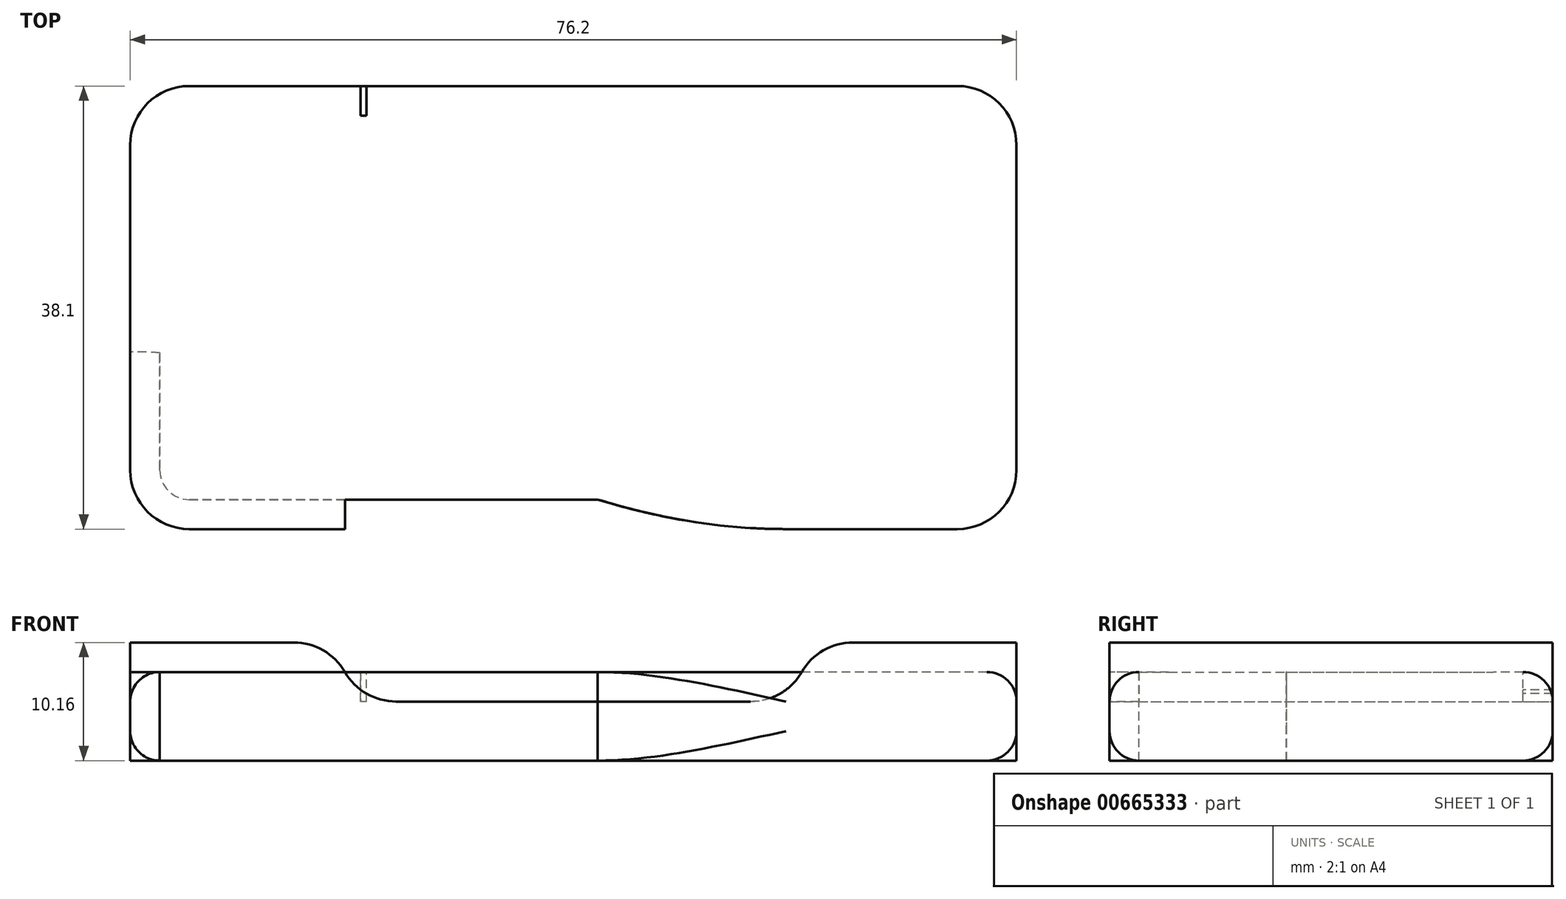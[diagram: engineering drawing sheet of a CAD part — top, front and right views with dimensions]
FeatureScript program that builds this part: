
annotation { "Feature Type Name" : "Feature", "Feature Type Description" : "" }
export const myFeature = defineFeature(function(context is Context, id is Id, definition is map)
    precondition{}
    {
        {
            var Q0;
            Q0=qCreatedBy(makeId("Top.planeOp"),FACE);
            var sketch = newSketch(context, id + "F0", { "sketchPlane" : qUnion([Q0])});
            skLineSegment(sketch, "E0.bottom", {"start": v(38.1, -19.05) * mm, "end": v(-38.1, -19.05) * mm});
            skLineSegment(sketch, "E0.top", {"start": v(38.1, 19.05) * mm, "end": v(-38.1, 19.05) * mm});
            skLineSegment(sketch, "E0.left", {"start": v(38.1, -19.05) * mm, "end": v(38.1, 19.05) * mm});
            skLineSegment(sketch, "E0.right", {"start": v(-38.1, -19.05) * mm, "end": v(-38.1, 19.05) * mm});
            skPoint(sketch, "E0.middle", {"position": v(0, 0) * mm});
            skSolve(sketch);
        }
        {
            var Q0;
            Q0=makeQuery(id+"F0.imprint","IMPRINT",FACE,{"disambiguationData":[TD([[makeQuery(id+"F0.imprint","IMPRINT",EDGE,{"derivedFrom":sQuery(id+"F0.wireOp",EDGE,"E0.bottom")}),-1.0]])]});
            extrude(context, id + "F1", {"entities" : qUnion([Q0]), "depth" : 10.16 * mm, "offsetDistance" : 25.4 * mm});
        }
        {
            var Q0;
            Q0=makeQuery(id+"F1.opExtrude","CAP_FACE",FACE,{"disambiguationData":[OSD([sQuery(id+"F0.wireOp",EDGE,"E0.bottom"),sQuery(id+"F0.wireOp",EDGE,"E0.top"),sQuery(id+"F0.wireOp",EDGE,"E0.left"),sQuery(id+"F0.wireOp",EDGE,"E0.right")])],"isStart":false});
            var sketch = newSketch(context, id + "F2", { "sketchPlane" : qUnion([Q0])});
            skLineSegment(sketch, "E1.bottom", {"start": v(20.32, -19.05) * mm, "end": v(-20.32, -19.05) * mm});
            skLineSegment(sketch, "E1.top", {"start": v(20.32, 19.05) * mm, "end": v(-20.32, 19.05) * mm});
            skLineSegment(sketch, "E1.left", {"start": v(20.32, -19.05) * mm, "end": v(20.32, 19.05) * mm});
            skLineSegment(sketch, "E1.right", {"start": v(-20.32, -19.05) * mm, "end": v(-20.32, 19.05) * mm});
            skPoint(sketch, "E1.middle", {"position": v(0, 0) * mm});
            skSolve(sketch);
        }
        {
            var Q0;
            Q0=makeQuery(id+"F2.imprint","IMPRINT",FACE,{"disambiguationData":[TD([[makeQuery(id+"F2.imprint","IMPRINT",EDGE,{"derivedFrom":sQuery(id+"F2.wireOp",EDGE,"E1.bottom")}),-1.0]])]});
            extrude(context, id + "F3", {"entities" : qUnion([Q0]), "operationType" : NewBodyOperationType.REMOVE, "oppositeDirection" : true, "depth" : 5.08 * mm, "offsetDistance" : 25.4 * mm});
        }
        {
            var Q0;
            Q0=makeQuery(id+"F1.opExtrude","SWEPT_EDGE",EDGE,{"disambiguationData":[OSD([sQuery(id+"F0.wireOp",EDGE,"E0.bottom"),sQuery(id+"F0.wireOp",EDGE,"E0.right")])]});
            var Q1;
            Q1=makeQuery(id+"F1.opExtrude","SWEPT_EDGE",EDGE,{"disambiguationData":[OSD([sQuery(id+"F0.wireOp",EDGE,"E0.top"),sQuery(id+"F0.wireOp",EDGE,"E0.right")])]});
            var Q2;
            Q2=makeQuery(id+"F1.opExtrude","SWEPT_EDGE",EDGE,{"disambiguationData":[OSD([sQuery(id+"F0.wireOp",EDGE,"E0.bottom"),sQuery(id+"F0.wireOp",EDGE,"E0.left")])]});
            var Q3;
            Q3=makeQuery(id+"F1.opExtrude","SWEPT_EDGE",EDGE,{"disambiguationData":[OSD([sQuery(id+"F0.wireOp",EDGE,"E0.top"),sQuery(id+"F0.wireOp",EDGE,"E0.left")])]});
            fillet(context, id + "F4", {"entities" : qUnion([Q0, Q1, Q2, Q3]), "radius" : 5.08 * mm, "tangentPropagation" : true, "allowEdgeOverflow" : false});
        }
        {
            var Q0;
            Q0=makeQuery(id+"F3.boolean.opBoolean","COPY",EDGE,{"derivedFrom":makeQuery(id+"F3.opExtrude","CAP_EDGE",EDGE,{"disambiguationData":[OSD([sQuery(id+"F2.wireOp",EDGE,"E1.right")])],"isStart":false})});
            var Q1;
            Q1=makeQuery(id+"F3.boolean.opBoolean","COPY",EDGE,{"derivedFrom":makeQuery(id+"F3.opExtrude","CAP_EDGE",EDGE,{"disambiguationData":[OSD([sQuery(id+"F2.wireOp",EDGE,"E1.left")])],"isStart":false})});
            fillet(context, id + "F5", {"entities" : qUnion([Q0, Q1]), "radius" : 5.08 * mm, "tangentPropagation" : true, "allowEdgeOverflow" : false});
        }
        {
            var Q0;
            {var subQ0=sQuery(id+"F0.wireOp",EDGE,"E0.bottom");var subQ1=sQuery(id+"F0.wireOp",EDGE,"E0.right");var subQ2=sQuery(id+"F0.wireOp",EDGE,"E0.top");var subQ3=sQuery(id+"F2.wireOp",EDGE,"E1.right");Q0=makeQuery(id+"F5.opFillet","BLEND_EDGE",EDGE,{"blendedFrom":[makeQuery(id+"F3.boolean.opBoolean","COPY",EDGE,{"derivedFrom":makeQuery(id+"F3.opExtrude","CAP_EDGE",EDGE,{"disambiguationData":[OSD([subQ3])],"isStart":false})}),makeQuery(id+"F3.boolean.opBoolean","SPLIT",FACE,{"disambiguationData":[TD([makeQuery(id+"F1.opExtrude","SWEPT_FACE",FACE,{"disambiguationData":[OSD([subQ1])]})])],"derivedFrom":makeQuery(id+"F1.opExtrude","CAP_FACE",FACE,{"disambiguationData":[OSD([subQ0,subQ2,sQuery(id+"F0.wireOp",EDGE,"E0.left"),subQ1])],"isStart":false})})],"blendedInto":[makeQuery(id+"F3.boolean.opBoolean","SPLIT",FACE,{"disambiguationData":[TD([makeQuery(id+"F1.opExtrude","SWEPT_FACE",FACE,{"disambiguationData":[OSD([subQ1])]})])],"derivedFrom":makeQuery(id+"F1.opExtrude","CAP_FACE",FACE,{"disambiguationData":[OSD([subQ0,subQ2,sQuery(id+"F0.wireOp",EDGE,"E0.left"),subQ1])],"isStart":false})})]});}
            var Q1;
            {var subQ0=sQuery(id+"F0.wireOp",EDGE,"E0.bottom");var subQ1=sQuery(id+"F0.wireOp",EDGE,"E0.top");var subQ2=sQuery(id+"F0.wireOp",EDGE,"E0.left");var subQ3=sQuery(id+"F2.wireOp",EDGE,"E1.left");Q1=makeQuery(id+"F5.opFillet","BLEND_EDGE",EDGE,{"blendedFrom":[makeQuery(id+"F3.boolean.opBoolean","COPY",EDGE,{"derivedFrom":makeQuery(id+"F3.opExtrude","CAP_EDGE",EDGE,{"disambiguationData":[OSD([subQ3])],"isStart":false})}),makeQuery(id+"F3.boolean.opBoolean","SPLIT",FACE,{"disambiguationData":[TD([makeQuery(id+"F1.opExtrude","SWEPT_FACE",FACE,{"disambiguationData":[OSD([subQ2])]})])],"derivedFrom":makeQuery(id+"F1.opExtrude","CAP_FACE",FACE,{"disambiguationData":[OSD([subQ0,subQ1,subQ2,sQuery(id+"F0.wireOp",EDGE,"E0.right")])],"isStart":false})})],"blendedInto":[makeQuery(id+"F3.boolean.opBoolean","SPLIT",FACE,{"disambiguationData":[TD([makeQuery(id+"F1.opExtrude","SWEPT_FACE",FACE,{"disambiguationData":[OSD([subQ2])]})])],"derivedFrom":makeQuery(id+"F1.opExtrude","CAP_FACE",FACE,{"disambiguationData":[OSD([subQ0,subQ1,subQ2,sQuery(id+"F0.wireOp",EDGE,"E0.right")])],"isStart":false})})]});}
            fillet(context, id + "F6", {"entities" : qUnion([Q0, Q1]), "radius" : 5.08 * mm, "tangentPropagation" : true, "allowEdgeOverflow" : false});
        }
        {
            var Q0;
            Q0=makeQuery(id+"F1.opExtrude","SWEPT_BODY",BODY,{"disambiguationData":[OSD([sQuery(id+"F0.wireOp",EDGE,"E0.bottom"),sQuery(id+"F0.wireOp",EDGE,"E0.top"),sQuery(id+"F0.wireOp",EDGE,"E0.left"),sQuery(id+"F0.wireOp",EDGE,"E0.right")])]});
            transform(context, id + "F7", {"entities" : qUnion([Q0]), "transformType" : TransformType.TRANSLATION_3D, "dx" : 0 * mm, "dy" : 0 * mm, "dz" : 0 * mm, "makeCopy" : true});
        }
        {
            var Q0;
            Q0=makeQuery(id+"F7.opPattern","COPY",BODY,{"derivedFrom":makeQuery(id+"F1.opExtrude","SWEPT_BODY",BODY,{"disambiguationData":[OSD([sQuery(id+"F0.wireOp",EDGE,"E0.bottom"),sQuery(id+"F0.wireOp",EDGE,"E0.top"),sQuery(id+"F0.wireOp",EDGE,"E0.left"),sQuery(id+"F0.wireOp",EDGE,"E0.right")])]}),"instanceName":"1"});
            deleteBodies(context, id + "F8", {"entities" : qUnion([Q0])});
        }
        {
            var Q0;
            Q0=makeQuery(id+"F1.opExtrude","CAP_FACE",FACE,{"disambiguationData":[OSD([sQuery(id+"F0.wireOp",EDGE,"E0.bottom"),sQuery(id+"F0.wireOp",EDGE,"E0.top"),sQuery(id+"F0.wireOp",EDGE,"E0.left"),sQuery(id+"F0.wireOp",EDGE,"E0.right")])],"isStart":true});
            var sketch = newSketch(context, id + "F9", { "sketchPlane" : qUnion([Q0])});
            skLineSegment(sketch, "E2.0", {"start": v(33.02, 19.05) * mm, "end": v(-33.02, 19.05) * mm});
            skArc(sketch, "E3.0", {"start": v(-33.02, 19.05) * mm, "mid": v(-36.61, 17.56) * mm, "end": v(-38.1, 13.97) * mm});
            skLineSegment(sketch, "E4.0", {"start": v(-38.1, 13.97) * mm, "end": v(-38.1, -13.97) * mm});
            skArc(sketch, "E5.0", {"start": v(-38.1, -13.97) * mm, "mid": v(-36.61, -17.56) * mm, "end": v(-33.02, -19.05) * mm});
            skLineSegment(sketch, "E6.0", {"start": v(33.02, -19.05) * mm, "end": v(-33.02, -19.05) * mm});
            skArc(sketch, "E7.0", {"start": v(33.02, -19.05) * mm, "mid": v(36.61, -17.56) * mm, "end": v(38.1, -13.97) * mm});
            skLineSegment(sketch, "E8.0", {"start": v(38.1, 13.97) * mm, "end": v(38.1, -13.97) * mm});
            skArc(sketch, "E9.0", {"start": v(38.1, 13.97) * mm, "mid": v(36.61, 17.56) * mm, "end": v(33.02, 19.05) * mm});
            skSolve(sketch);
        }
        {
            var Q0;
            Q0=qSketchRegion(id+"F9",true);
            extrude(context, id + "F10", {"entities" : qUnion([Q0]), "oppositeDirection" : true, "depth" : 7.62 * mm, "offsetDistance" : 25.4 * mm});
        }
        {
            var Q0;
            Q0=makeQuery(id+"F10.opExtrude","CAP_EDGE",EDGE,{"disambiguationData":[OSD([sQuery(id+"F9.wireOp",EDGE,"E2.0")])],"isStart":false});
            var Q1;
            Q1=makeQuery(id+"F10.opExtrude","CAP_EDGE",EDGE,{"disambiguationData":[OSD([sQuery(id+"F9.wireOp",EDGE,"E2.0")])],"isStart":true});
            fillet(context, id + "F11", {"entities" : qUnion([Q0, Q1]), "radius" : 2.54 * mm, "tangentPropagation" : true, "allowEdgeOverflow" : false});
        }
        {
            var Q0;
            Q0=makeQuery(id+"F10.opExtrude","CAP_FACE",FACE,{"disambiguationData":[OSD([sQuery(id+"F9.wireOp",EDGE,"E2.0"),sQuery(id+"F9.wireOp",EDGE,"E3.0"),sQuery(id+"F9.wireOp",EDGE,"E4.0"),sQuery(id+"F9.wireOp",EDGE,"E5.0"),sQuery(id+"F9.wireOp",EDGE,"E6.0"),sQuery(id+"F9.wireOp",EDGE,"E7.0"),sQuery(id+"F9.wireOp",EDGE,"E8.0"),sQuery(id+"F9.wireOp",EDGE,"E9.0")])],"isStart":false});
            var sketch = newSketch(context, id + "F12", { "sketchPlane" : qUnion([Q0])});
            skLineSegment(sketch, "E10.bottom", {"start": v(17.78, -19.05) * mm, "end": v(-17.78, -19.05) * mm, "construction": true});
            skLineSegment(sketch, "E10.top", {"start": v(17.78, 19.05) * mm, "end": v(-17.78, 19.05) * mm, "construction": true});
            skLineSegment(sketch, "E10.left", {"start": v(17.78, -19.05) * mm, "end": v(17.78, 19.05) * mm});
            skLineSegment(sketch, "E10.right", {"start": v(-17.78, -19.05) * mm, "end": v(-17.78, 19.05) * mm});
            skPoint(sketch, "E10.middle", {"position": v(0, 0) * mm});
            skLineSegment(sketch, "E11.bottom", {"start": v(-17.78, 19.05) * mm, "end": v(-18.29, 19.05) * mm});
            skLineSegment(sketch, "E11.top", {"start": v(-17.78, -19.05) * mm, "end": v(-18.29, -19.05) * mm});
            skLineSegment(sketch, "E11.left", {"start": v(-17.78, 19.05) * mm, "end": v(-17.78, -19.05) * mm});
            skLineSegment(sketch, "E11.right", {"start": v(-18.29, 19.05) * mm, "end": v(-18.29, -19.05) * mm});
            skSolve(sketch);
        }
        {
            var Q0;
            {var subQ0=sQuery(id+"F12.wireOp",EDGE,"E11.left");var subQ1=sQuery(id+"F9.wireOp",EDGE,"E6.0");var subQ2=sQuery(id+"F9.wireOp",EDGE,"E2.0");var subQ3=makeQuery(id+"F10.opExtrude","CAP_FACE",FACE,{"disambiguationData":[OSD([subQ2,sQuery(id+"F9.wireOp",EDGE,"E3.0"),sQuery(id+"F9.wireOp",EDGE,"E4.0"),sQuery(id+"F9.wireOp",EDGE,"E5.0"),subQ1,sQuery(id+"F9.wireOp",EDGE,"E7.0"),sQuery(id+"F9.wireOp",EDGE,"E8.0"),sQuery(id+"F9.wireOp",EDGE,"E9.0")])],"isStart":false});var subQ4=makeQuery(id+"F11.opFillet","BLEND_EDGE",EDGE,{"blendedFrom":[makeQuery(id+"F10.opExtrude","CAP_EDGE",EDGE,{"disambiguationData":[OSD([subQ1])],"isStart":false}),subQ3],"blendedInto":[subQ3]});var subQ5=makeQuery(id+"F12.imprint","INTERSECT",VERTEX,{"derivedFrom":[subQ4,subQ0]});Q0=makeQuery(id+"F12.imprint","IMPRINT",FACE,{"disambiguationData":[TD([[makeQuery(id+"F12.imprint","IMPRINT",EDGE,{"disambiguationData":[TD([[subQ5,-1.0]])],"derivedFrom":subQ0}),-1.0]])]});}
            var Q1;
            {var subQ0=sQuery(id+"F12.wireOp",EDGE,"E11.bottom");Q1=makeQuery(id+"F12.imprint","IMPRINT",FACE,{"disambiguationData":[TD([[makeQuery(id+"F12.imprint","IMPRINT",EDGE,{"derivedFrom":subQ0}),1.0]])]});}
            var Q2;
            {var subQ0=sQuery(id+"F12.wireOp",EDGE,"E11.top");Q2=makeQuery(id+"F12.imprint","IMPRINT",FACE,{"disambiguationData":[TD([[makeQuery(id+"F12.imprint","IMPRINT",EDGE,{"derivedFrom":subQ0}),-1.0]])]});}
            extrude(context, id + "F13", {"entities" : qUnion([Q0, Q1, Q2]), "operationType" : NewBodyOperationType.REMOVE, "oppositeDirection" : true, "depth" : 2.54 * mm, "offsetDistance" : 25.4 * mm});
        }
        {
            var Q0;
            Q0=makeQuery(id+"F10.opExtrude","SWEPT_BODY",BODY,{"disambiguationData":[OSD([sQuery(id+"F9.wireOp",EDGE,"E2.0"),sQuery(id+"F9.wireOp",EDGE,"E3.0"),sQuery(id+"F9.wireOp",EDGE,"E4.0"),sQuery(id+"F9.wireOp",EDGE,"E5.0"),sQuery(id+"F9.wireOp",EDGE,"E6.0"),sQuery(id+"F9.wireOp",EDGE,"E7.0"),sQuery(id+"F9.wireOp",EDGE,"E8.0"),sQuery(id+"F9.wireOp",EDGE,"E9.0")])]});
            transform(context, id + "F14", {"entities" : qUnion([Q0]), "transformType" : TransformType.TRANSLATION_3D, "dx" : 0 * mm, "dy" : 0 * mm, "dz" : 0 * mm, "makeCopy" : true});
        }
        {
            var Q0;
            {var subQ0=sQuery(id+"F9.wireOp",EDGE,"E2.0");var subQ2=sQuery(id+"F12.wireOp",EDGE,"E11.left");var subQ3=makeQuery(id+"F13.opExtrude","SWEPT_FACE",FACE,{"disambiguationData":[OSD([subQ2])]});var subQ4=sQuery(id+"F9.wireOp",EDGE,"E6.0");var subQ6=sQuery(id+"F9.wireOp",EDGE,"E8.0");var subQ7=sQuery(id+"F9.wireOp",EDGE,"E7.0");var subQ8=sQuery(id+"F9.wireOp",EDGE,"E9.0");Q0=makeQuery(id+"F14.opPattern","COPY",FACE,{"derivedFrom":makeQuery(id+"FZbfRHft5HWekoC_2.1.F13.boolean.opBoolean","SPLIT",FACE,{"disambiguationData":[TD([makeQuery(id+"F13.boolean.opBoolean","COPY",FACE,{"derivedFrom":subQ3})])],"derivedFrom":makeQuery(id+"F13.boolean.opBoolean","SPLIT",FACE,{"disambiguationData":[TD([subQ3])],"derivedFrom":makeQuery(id+"F10.opExtrude","CAP_FACE",FACE,{"disambiguationData":[OSD([subQ0,sQuery(id+"F9.wireOp",EDGE,"E3.0"),sQuery(id+"F9.wireOp",EDGE,"E4.0"),sQuery(id+"F9.wireOp",EDGE,"E5.0"),subQ4,subQ7,subQ6,subQ8])],"isStart":false})})}),"instanceName":"1"});}
            var sketch = newSketch(context, id + "F15", { "sketchPlane" : qUnion([Q0])});
            skLineSegment(sketch, "E12.0", {"start": v(-38.1, -13.97) * mm, "end": v(-38.1, 13.97) * mm});
            skPoint(sketch, "E13.0", {"position": v(18.29, -19.05) * mm});
            skFitSpline(sketch, "E14", {"points": [v(-38.1, -3.81) * mm, v(18.29, -19.05) * mm], "startDerivative": vector(59.44, 0) * mm, "endDerivative": vector(68.58, 0) * mm});
            skPoint(sketch, "E15.0", {"position": v(-33.02, 19.05) * mm});
            skLineSegment(sketch, "E16", {"start": v(-33.02, 19.05) * mm, "end": v(-45.72, 19.05) * mm});
            skLineSegment(sketch, "E17", {"start": v(-38.1, -3.81) * mm, "end": v(-38.1, -19.05) * mm});
            skLineSegment(sketch, "E18", {"start": v(-38.1, -19.05) * mm, "end": v(18.29, -19.05) * mm});
            skSolve(sketch);
        }
        {
            var Q0;
            {var subQ0=sQuery(id+"F15.wireOp",EDGE,"E18");Q0=makeQuery(id+"F15.imprint","IMPRINT",FACE,{"disambiguationData":[TD([[makeQuery(id+"F15.imprint","IMPRINT",EDGE,{"derivedFrom":subQ0}),1.0]])]});}
            var Q1;
            {var subQ0=sQuery(id+"F15.wireOp",EDGE,"E14");var subQ1=sQuery(id+"F12.wireOp",EDGE,"E11.left");var subQ2=makeQuery(id+"F14.opPattern","COPY",EDGE,{"derivedFrom":makeQuery(id+"F13.boolean.opBoolean","COPY",EDGE,{"derivedFrom":makeQuery(id+"F13.opExtrude","CAP_EDGE",EDGE,{"disambiguationData":[OSD([subQ1])],"isStart":true})}),"instanceName":"1"});var subQ3=makeQuery(id+"F15.imprint","INTERSECT",VERTEX,{"derivedFrom":[subQ2,subQ0]});Q1=makeQuery(id+"F15.imprint","IMPRINT",FACE,{"disambiguationData":[TD([[makeQuery(id+"F15.imprint","IMPRINT",EDGE,{"disambiguationData":[TD([[subQ3,-1.0]])],"derivedFrom":subQ0}),-1.0]])]});}
            extrude(context, id + "F16", {"entities" : qUnion([Q0, Q1]), "operationType" : NewBodyOperationType.REMOVE, "endBound" : BoundingType.THROUGH_ALL, "oppositeDirection" : true, "depth" : 25.4 * mm, "offsetDistance" : 25.4 * mm});
        }
        {
            var Q0;
            Q0=makeQuery(id+"F14.opPattern","COPY",BODY,{"derivedFrom":makeQuery(id+"F10.opExtrude","SWEPT_BODY",BODY,{"disambiguationData":[OSD([sQuery(id+"F9.wireOp",EDGE,"E2.0"),sQuery(id+"F9.wireOp",EDGE,"E3.0"),sQuery(id+"F9.wireOp",EDGE,"E4.0"),sQuery(id+"F9.wireOp",EDGE,"E5.0"),sQuery(id+"F9.wireOp",EDGE,"E6.0"),sQuery(id+"F9.wireOp",EDGE,"E7.0"),sQuery(id+"F9.wireOp",EDGE,"E8.0"),sQuery(id+"F9.wireOp",EDGE,"E9.0")])]}),"instanceName":"1"});
            deleteBodies(context, id + "F17", {"entities" : qUnion([Q0])});
        }
    });
